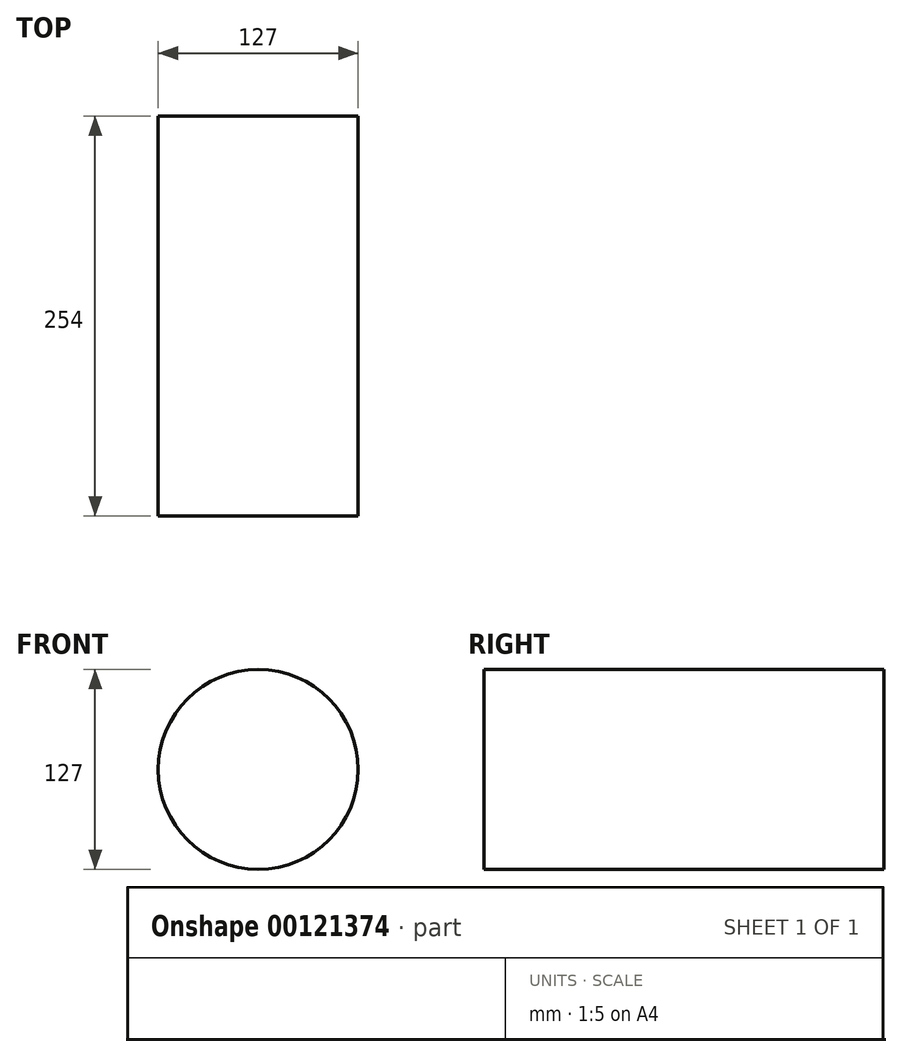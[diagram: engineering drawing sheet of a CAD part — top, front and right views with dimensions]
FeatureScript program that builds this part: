
annotation { "Feature Type Name" : "Feature", "Feature Type Description" : "" }
export const myFeature = defineFeature(function(context is Context, id is Id, definition is map)
    precondition{}
    {
        {
            var Q0;
            Q0=qCreatedBy(makeId("Front.planeOp"),FACE);
            var sketch = newSketch(context, id + "F0", { "sketchPlane" : qUnion([Q0])});
            skCircle(sketch, "E0", {"center": v(0, 0) * mm, "radius": 63.5 * mm});
            skSolve(sketch);
        }
        {
            var Q0;
            Q0=makeQuery(id+"F0.imprint","IMPRINT",FACE,{"disambiguationData":[TD([[makeQuery(id+"F0.imprint","IMPRINT",EDGE,{"derivedFrom":sQuery(id+"F0.wireOp",EDGE,"E0")}),1.0]])]});
            extrude(context, id + "F1", {"entities" : qUnion([Q0]), "depth" : 254 * mm});
        }
    });
